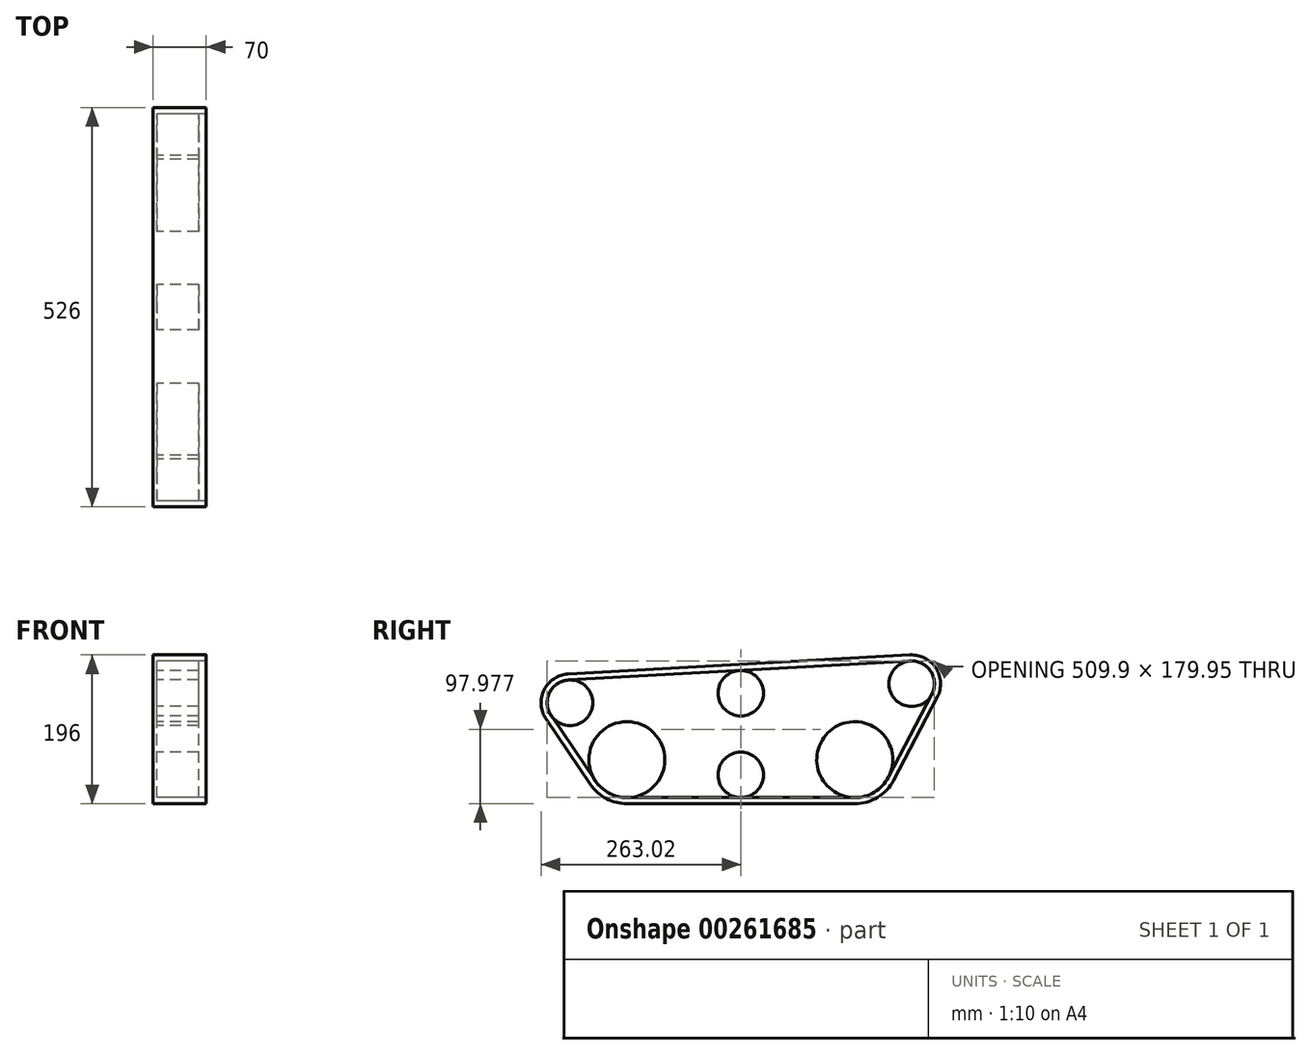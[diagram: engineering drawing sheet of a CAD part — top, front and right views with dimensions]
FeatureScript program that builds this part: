
annotation { "Feature Type Name" : "Feature", "Feature Type Description" : "" }
export const myFeature = defineFeature(function(context is Context, id is Id, definition is map)
    precondition{}
    {
        {
            var Q0;
            Q0=qCreatedBy(makeId("Right.planeOp"),FACE);
            var sketch = newSketch(context, id + "F0", { "sketchPlane" : qUnion([Q0])});
            skCircle(sketch, "E0", {"center": v(0, 0) * mm, "radius": 50 * mm});
            skCircle(sketch, "E1", {"center": v(300, 0) * mm, "radius": 50 * mm});
            skCircle(sketch, "E2", {"center": v(150, -20) * mm, "radius": 30 * mm});
            skCircle(sketch, "E3", {"center": v(375, 100) * mm, "radius": 30 * mm});
            skCircle(sketch, "E4", {"center": v(-75, 75) * mm, "radius": 30 * mm});
            skCircle(sketch, "E5", {"center": v(150, 87.5) * mm, "radius": 30 * mm});
            skLineSegment(sketch, "E6", {"start": v(-76.66, 104.95) * mm, "end": v(373.34, 129.95) * mm});
            skLineSegment(sketch, "E7", {"start": v(0, -50) * mm, "end": v(300, -50) * mm});
            skLineSegment(sketch, "E8", {"start": v(344.28, -23.21) * mm, "end": v(401.57, 86.07) * mm});
            skLineSegment(sketch, "E9", {"start": v(-99.83, 58.17) * mm, "end": v(-41.39, -28.05) * mm});
            skLineSegment(sketch, "E10.0", {"start": v(-77.1, 112.94) * mm, "end": v(372.9, 137.94) * mm});
            skArc(sketch, "E11.0", {"start": v(408.66, 82.36) * mm, "mid": v(406.96, 120.56) * mm, "end": v(372.9, 137.94) * mm});
            skLineSegment(sketch, "E12.0", {"start": v(351.37, -26.93) * mm, "end": v(408.66, 82.36) * mm});
            skArc(sketch, "E13.0", {"start": v(300, -58) * mm, "mid": v(330.02, -49.63) * mm, "end": v(351.37, -26.93) * mm});
            skLineSegment(sketch, "E14.0", {"start": v(0, -58) * mm, "end": v(300, -58) * mm});
            skArc(sketch, "E15.0", {"start": v(-48, -32.54) * mm, "mid": v(-27.17, -51.24) * mm, "end": v(0, -58) * mm});
            skLineSegment(sketch, "E16.0", {"start": v(-106.45, 53.68) * mm, "end": v(-48, -32.54) * mm});
            skArc(sketch, "E17.0", {"start": v(-77.1, 112.94) * mm, "mid": v(-109.05, 91.86) * mm, "end": v(-106.45, 53.68) * mm});
            skSolve(sketch);
        }
        {
            var Q0;
            {var subQ0=sQuery(id+"F0.wireOp",EDGE,"E0");var subQ1=makeQuery(id+"F0.imprint","INTERSECT",VERTEX,{"derivedFrom":[subQ0,sQuery(id+"F0.wireOp",EDGE,"E7")]});Q0=makeQuery(id+"F0.imprint","IMPRINT",FACE,{"disambiguationData":[TD([[makeQuery(id+"F0.imprint","IMPRINT",EDGE,{"disambiguationData":[TD([[subQ1,1.0]])],"derivedFrom":subQ0}),1.0]])]});}
            var Q1;
            {var subQ0=sQuery(id+"F0.wireOp",EDGE,"E4");var subQ1=makeQuery(id+"F0.imprint","INTERSECT",VERTEX,{"derivedFrom":[subQ0,sQuery(id+"F0.wireOp",EDGE,"E6")]});Q1=makeQuery(id+"F0.imprint","IMPRINT",FACE,{"disambiguationData":[TD([[makeQuery(id+"F0.imprint","IMPRINT",EDGE,{"disambiguationData":[TD([[subQ1,-1.0]])],"derivedFrom":subQ0}),1.0]])]});}
            var Q2;
            Q2=makeQuery(id+"F0.imprint","IMPRINT",FACE,{"disambiguationData":[TD([[makeQuery(id+"F0.imprint","IMPRINT",EDGE,{"derivedFrom":sQuery(id+"F0.wireOp",EDGE,"E5")}),1.0]])]});
            var Q3;
            {var subQ0=sQuery(id+"F0.wireOp",EDGE,"E1");var subQ1=makeQuery(id+"F0.imprint","INTERSECT",VERTEX,{"derivedFrom":[subQ0,sQuery(id+"F0.wireOp",EDGE,"E7")]});Q3=makeQuery(id+"F0.imprint","IMPRINT",FACE,{"disambiguationData":[TD([[makeQuery(id+"F0.imprint","IMPRINT",EDGE,{"disambiguationData":[TD([[subQ1,-1.0]])],"derivedFrom":subQ0}),1.0]])]});}
            var Q4;
            {var subQ0=sQuery(id+"F0.wireOp",EDGE,"E3");var subQ1=makeQuery(id+"F0.imprint","INTERSECT",VERTEX,{"derivedFrom":[subQ0,sQuery(id+"F0.wireOp",EDGE,"E6")]});Q4=makeQuery(id+"F0.imprint","IMPRINT",FACE,{"disambiguationData":[TD([[makeQuery(id+"F0.imprint","IMPRINT",EDGE,{"disambiguationData":[TD([[subQ1,-1.0]])],"derivedFrom":subQ0}),1.0]])]});}
            var Q5;
            Q5=makeQuery(id+"F0.imprint","IMPRINT",FACE,{"disambiguationData":[TD([[makeQuery(id+"F0.imprint","IMPRINT",EDGE,{"derivedFrom":sQuery(id+"F0.wireOp",EDGE,"E2")}),1.0]])]});
            extrude(context, id + "F1", {"entities" : qUnion([Q0, Q1, Q2, Q3, Q4, Q5]), "depth" : 40 * mm, "hasSecondDirection" : true, "secondDirectionOppositeDirection" : true, "secondDirectionDepth" : 15 * mm});
        }
        {
            var Q0;
            {var subQ13=sQuery(id+"F0.wireOp",EDGE,"E8");Q0=makeQuery(id+"F0.imprint","IMPRINT",FACE,{"disambiguationData":[TD([[makeQuery(id+"F0.imprint","IMPRINT",EDGE,{"derivedFrom":subQ13}),-1.0]])]});}
            extrude(context, id + "F2", {"entities" : qUnion([Q0]), "depth" : 50 * mm, "hasSecondDirection" : true, "secondDirectionOppositeDirection" : true, "secondDirectionDepth" : 20 * mm});
        }
    });
